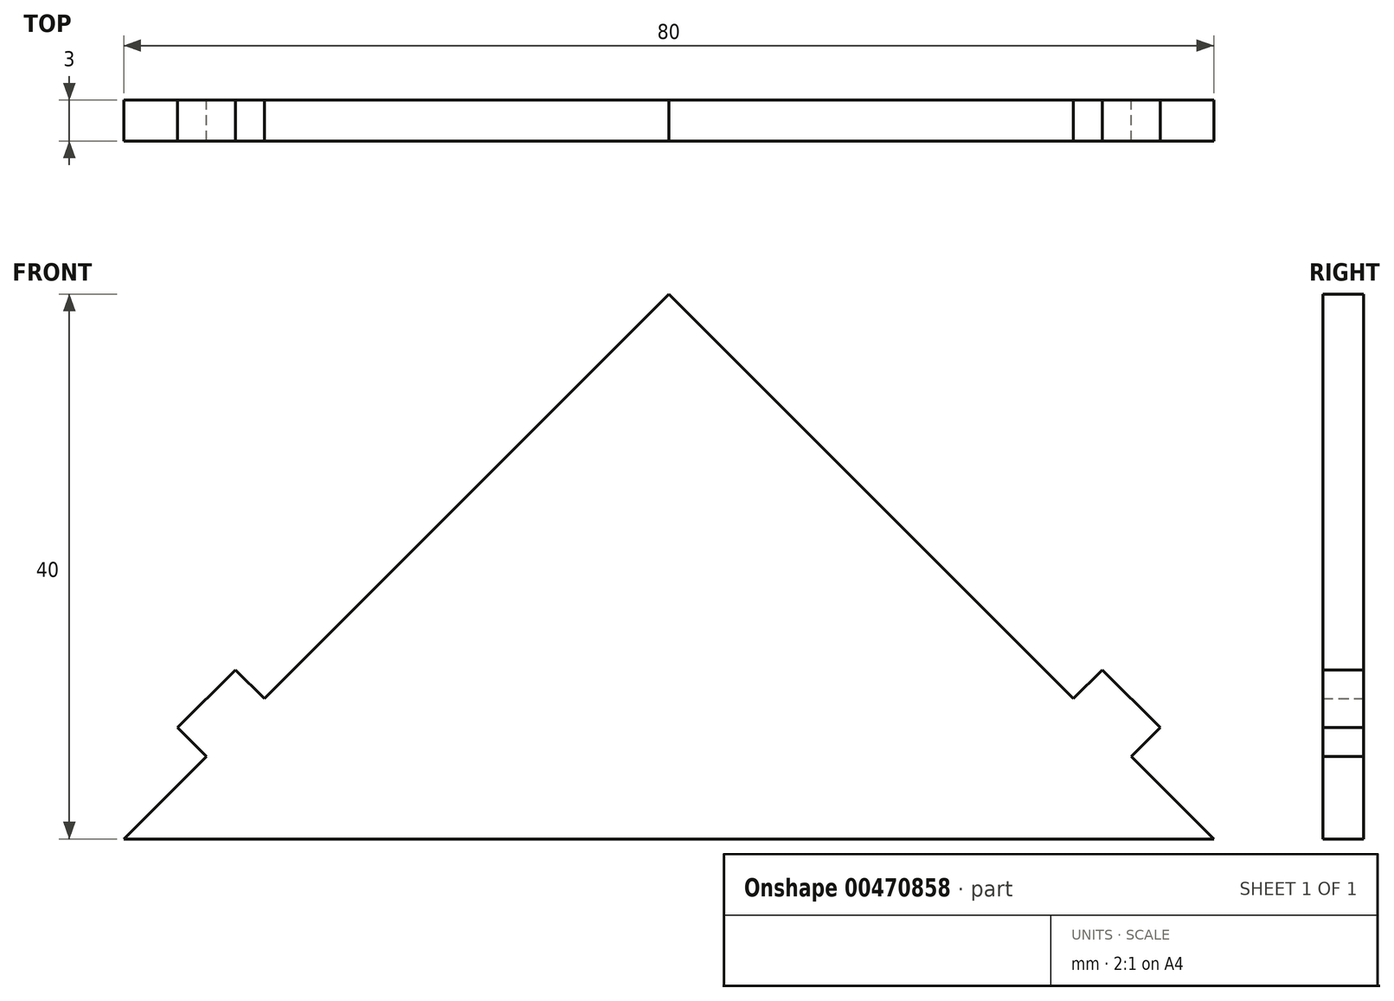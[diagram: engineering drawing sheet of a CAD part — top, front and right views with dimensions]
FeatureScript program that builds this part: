
annotation { "Feature Type Name" : "Feature", "Feature Type Description" : "" }
export const myFeature = defineFeature(function(context is Context, id is Id, definition is map)
    precondition{}
    {
        {
            assignVariable(context, id + "F0", {"name" : "WoodWidth", "anyValue" : 3});
        }
        {
            var Q0;
            Q0=qCreatedBy(makeId("Front.planeOp"),FACE);
            var sketch = newSketch(context, id + "F1", { "sketchPlane" : qUnion([Q0])});
            skLineSegment(sketch, "E0", {"start": v(-40, 0) * mm, "end": v(0, 40) * mm});
            skLineSegment(sketch, "E1", {"start": v(0, 40) * mm, "end": v(40, 0) * mm});
            skLineSegment(sketch, "E2", {"start": v(40, 0) * mm, "end": v(-40, 0) * mm});
            skLineSegment(sketch, "E3", {"start": v(-36.06, 8.18) * mm, "end": v(-31.82, 12.42) * mm});
            skLineSegment(sketch, "E4", {"start": v(-31.82, 12.42) * mm, "end": v(-29.7, 10.3) * mm});
            skLineSegment(sketch, "E5", {"start": v(-36.06, 8.18) * mm, "end": v(-33.94, 6.06) * mm});
            skLineSegment(sketch, "E6", {"start": v(33.94, 6.06) * mm, "end": v(36.06, 8.18) * mm});
            skLineSegment(sketch, "E7", {"start": v(36.06, 8.18) * mm, "end": v(31.82, 12.42) * mm});
            skLineSegment(sketch, "E8", {"start": v(31.82, 12.42) * mm, "end": v(29.7, 10.3) * mm});
            skSolve(sketch);
        }
        {
            var Q0;
            {var subQ6=sQuery(id+"F1.wireOp",EDGE,"E2");Q0=makeQuery(id+"F1.imprint","IMPRINT",FACE,{"disambiguationData":[TD([[makeQuery(id+"F1.imprint","IMPRINT",EDGE,{"derivedFrom":subQ6}),-1.0]])]});}
            var Q1;
            {var subQ0=sQuery(id+"F1.wireOp",EDGE,"E6");Q1=makeQuery(id+"F1.imprint","IMPRINT",FACE,{"disambiguationData":[TD([[makeQuery(id+"F1.imprint","IMPRINT",EDGE,{"derivedFrom":subQ0}),1.0]])]});}
            var Q2;
            Q2=makeQuery(id+"F1.imprint","IMPRINT",FACE,{"disambiguationData":[TD([[makeQuery(id+"F1.imprint","IMPRINT",EDGE,{"derivedFrom":sQuery(id+"F1.wireOp",EDGE,"E3")}),-1.0]])]});
            extrude(context, id + "F2", {"entities" : qUnion([Q0, Q1, Q2]), "depth" : (getVariable(context, 'WoodWidth')) * mm});
        }
    });
